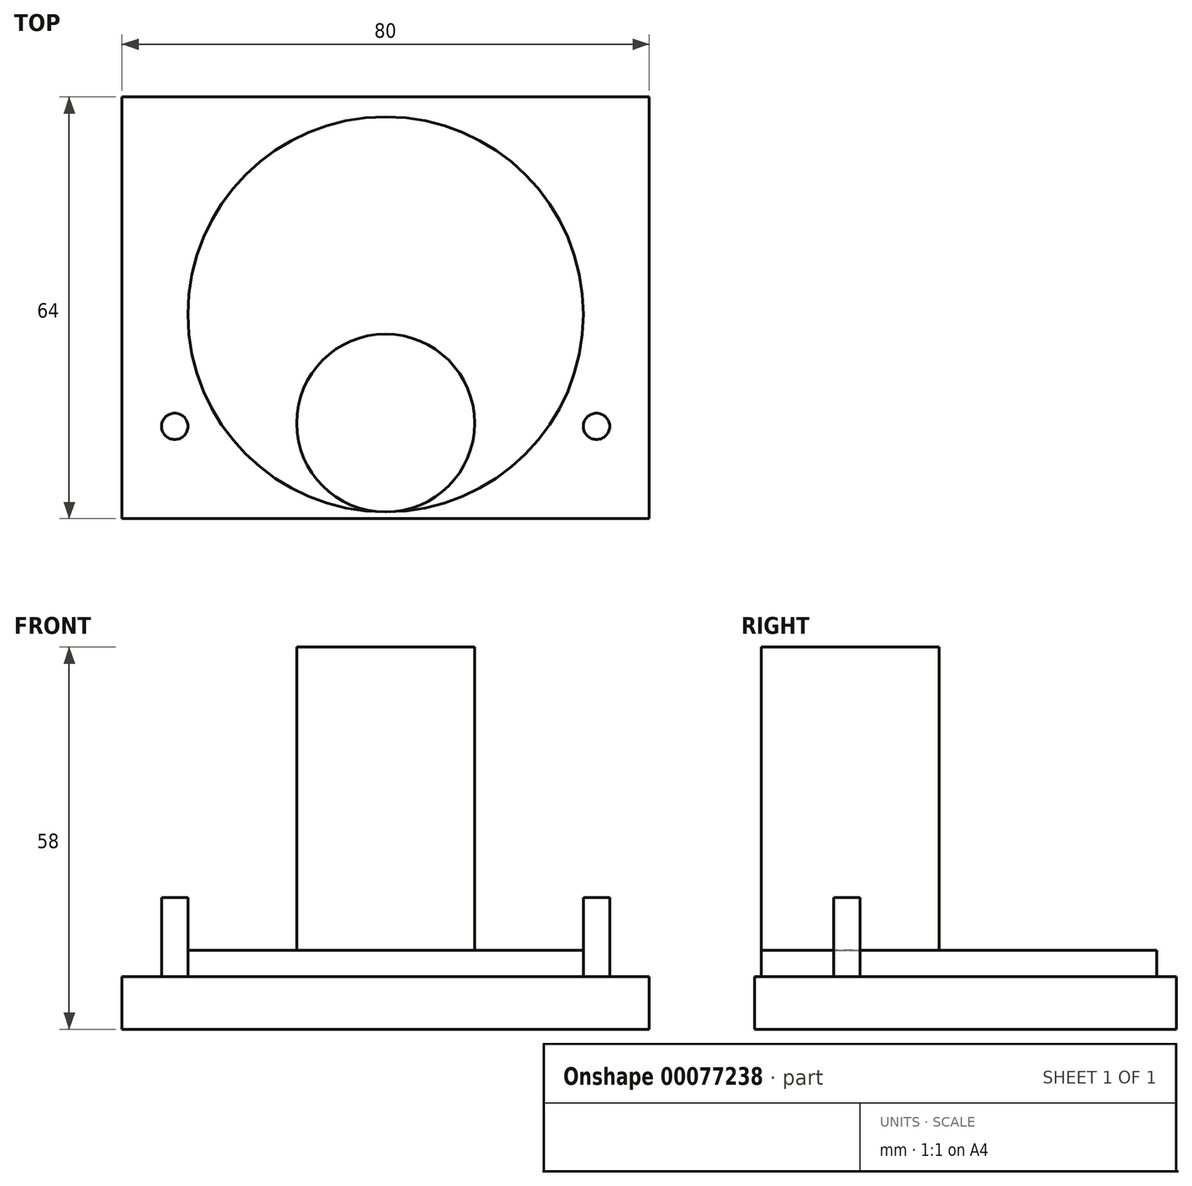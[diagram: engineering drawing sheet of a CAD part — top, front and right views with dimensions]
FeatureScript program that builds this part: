
annotation { "Feature Type Name" : "Feature", "Feature Type Description" : "" }
export const myFeature = defineFeature(function(context is Context, id is Id, definition is map)
    precondition{}
    {
        {
            var Q0;
            Q0=qCreatedBy(makeId("Top.planeOp"),FACE);
            var sketch = newSketch(context, id + "F0", { "sketchPlane" : qUnion([Q0])});
            skCircle(sketch, "E0", {"center": v(0, 0) * mm, "radius": 30 * mm});
            skSolve(sketch);
        }
        {
            var Q0;
            Q0=makeQuery(id+"F0.imprint","IMPRINT",FACE,{"disambiguationData":[TD([[makeQuery(id+"F0.imprint","IMPRINT",EDGE,{"derivedFrom":sQuery(id+"F0.wireOp",EDGE,"E0")}),1.0]])]});
            extrude(context, id + "F1", {"entities" : qUnion([Q0]), "oppositeDirection" : true, "depth" : 4 * mm});
        }
        {
            var Q0;
            Q0=makeQuery(id+"F1.opExtrude","CAP_FACE",FACE,{"disambiguationData":[OSD([sQuery(id+"F0.wireOp",EDGE,"E0")])],"isStart":false});
            var sketch = newSketch(context, id + "F2", { "sketchPlane" : qUnion([Q0])});
            skLineSegment(sketch, "E1.bottom", {"start": v(-40, -33) * mm, "end": v(40, -33) * mm});
            skLineSegment(sketch, "E1.top", {"start": v(-40, 31) * mm, "end": v(40, 31) * mm});
            skLineSegment(sketch, "E1.left", {"start": v(-40, -33) * mm, "end": v(-40, 31) * mm});
            skLineSegment(sketch, "E1.right", {"start": v(40, -33) * mm, "end": v(40, 31) * mm});
            skLineSegment(sketch, "E2", {"start": v(0, 31) * mm, "end": v(0, 30) * mm});
            skSolve(sketch);
        }
        {
            var Q0;
            Q0=makeQuery(id+"F2.imprint","IMPRINT",FACE,{"disambiguationData":[TD([[makeQuery(id+"F2.imprint","IMPRINT",EDGE,{"derivedFrom":sQuery(id+"F2.wireOp",EDGE,"E1.bottom")}),1.0]])]});
            var Q1;
            Q1=makeQuery(id+"F2.imprint","IMPRINT",FACE,{"disambiguationData":[TD([[makeQuery(id+"F2.imprint","IMPRINT",EDGE,{"derivedFrom":makeQuery(id+"F1.opExtrude","CAP_EDGE",EDGE,{"disambiguationData":[OSD([sQuery(id+"F0.wireOp",EDGE,"E0")])],"isStart":false})}),-1.0]])]});
            extrude(context, id + "F3", {"entities" : qUnion([Q0, Q1]), "operationType" : NewBodyOperationType.ADD, "depth" : 8 * mm});
        }
        {
            var Q0;
            Q0=makeQuery(id+"F3.opExtrude","CAP_FACE",FACE,{"disambiguationData":[OSD([sQuery(id+"F2.wireOp",EDGE,"E1.bottom"),sQuery(id+"F2.wireOp",EDGE,"E1.top"),sQuery(id+"F2.wireOp",EDGE,"E1.left"),sQuery(id+"F2.wireOp",EDGE,"E1.right")])],"isStart":true});
            var sketch = newSketch(context, id + "F4", { "sketchPlane" : qUnion([Q0])});
            skCircle(sketch, "E3", {"center": v(-32, -17) * mm, "radius": 2 * mm});
            skCircle(sketch, "E4", {"center": v(32, -17) * mm, "radius": 2 * mm});
            skLineSegment(sketch, "E5", {"start": v(0, 0) * mm, "end": v(0, -36.6) * mm});
            skSolve(sketch);
        }
        {
            var Q0;
            Q0 = qSketchRegion(id + "F4", true);
            extrude(context, id + "F5", {"entities" : qUnion([Q0]), "operationType" : NewBodyOperationType.ADD, "depth" : 12 * mm});
        }
        {
            var Q0;
            Q0=makeQuery(id+"F3.opExtrude","CAP_FACE",FACE,{"disambiguationData":[OSD([sQuery(id+"F2.wireOp",EDGE,"E1.bottom"),sQuery(id+"F2.wireOp",EDGE,"E1.top"),sQuery(id+"F2.wireOp",EDGE,"E1.left"),sQuery(id+"F2.wireOp",EDGE,"E1.right")])],"isStart":true});
            var sketch = newSketch(context, id + "F6", { "sketchPlane" : qUnion([Q0])});
            skCircle(sketch, "E6", {"center": v(0, -16.5) * mm, "radius": 13.5 * mm});
            skSolve(sketch);
        }
        {
            var Q0;
            Q0 = qSketchRegion(id + "F6", true);
            extrude(context, id + "F7", {"entities" : qUnion([Q0]), "operationType" : NewBodyOperationType.ADD, "depth" : 50 * mm});
        }
    });
